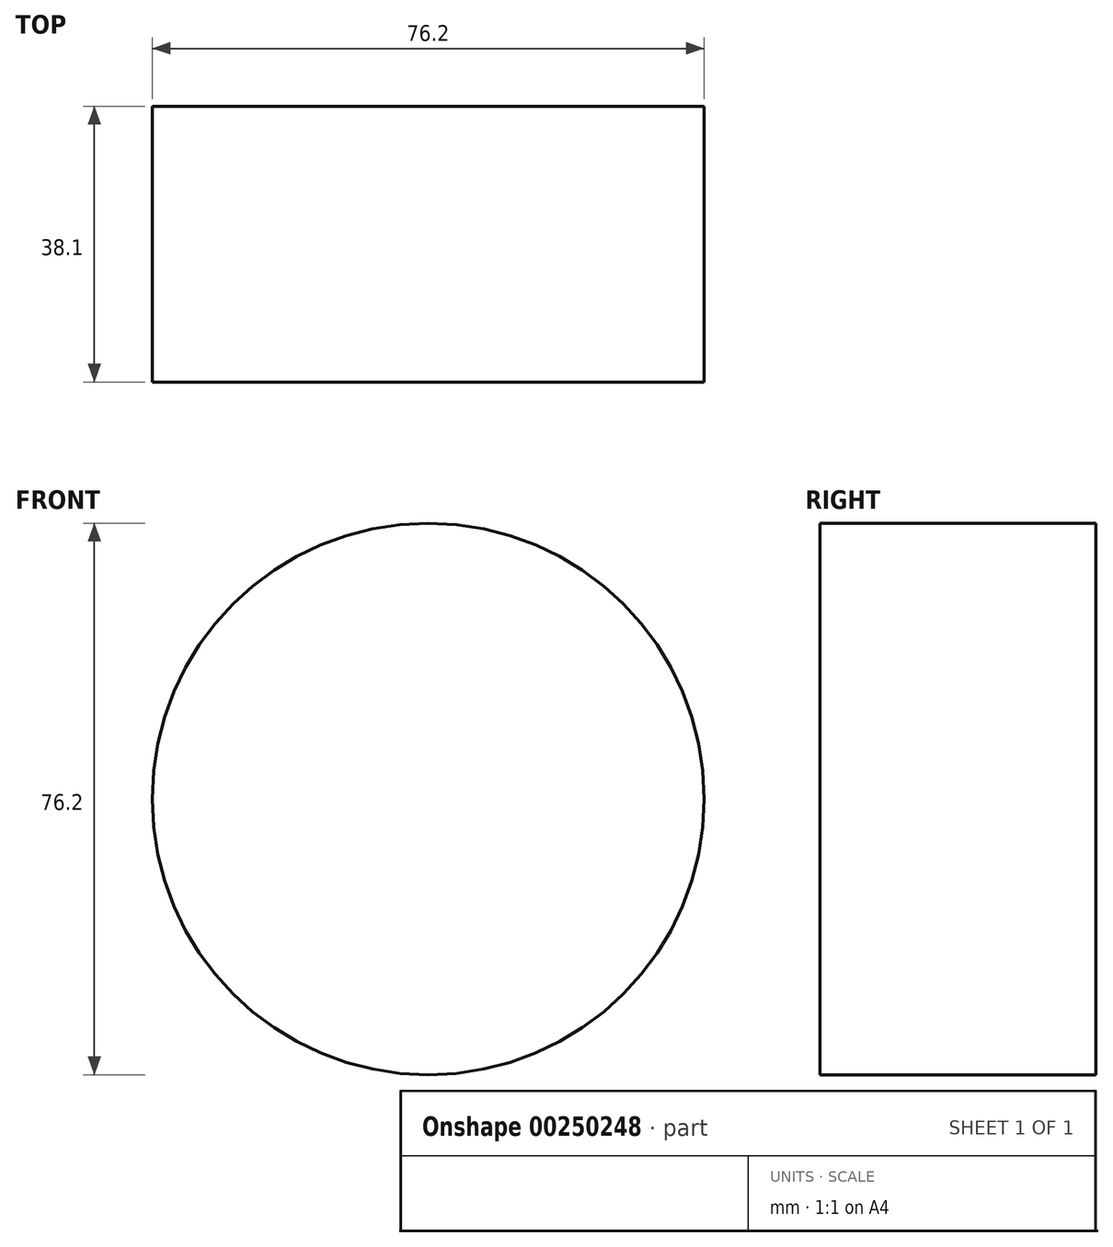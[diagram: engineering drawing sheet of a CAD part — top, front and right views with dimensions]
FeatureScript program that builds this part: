
annotation { "Feature Type Name" : "Feature", "Feature Type Description" : "" }
export const myFeature = defineFeature(function(context is Context, id is Id, definition is map)
    precondition{}
    {
        {
            var Q0;
            Q0=qCreatedBy(makeId("Front.planeOp"),FACE);
            var sketch = newSketch(context, id + "F0", { "sketchPlane" : qUnion([Q0])});
            skCircle(sketch, "E0", {"center": v(0, 0) * mm, "radius": 38.1 * mm});
            skSolve(sketch);
        }
        {
            var Q0;
            Q0=makeQuery(id+"F0.imprint","IMPRINT",FACE,{"disambiguationData":[TD([[makeQuery(id+"F0.imprint","IMPRINT",EDGE,{"derivedFrom":sQuery(id+"F0.wireOp",EDGE,"E0")}),1.0]])]});
            extrude(context, id + "F1", {"entities" : qUnion([Q0]), "depth" : 38.1 * mm});
        }
    });
